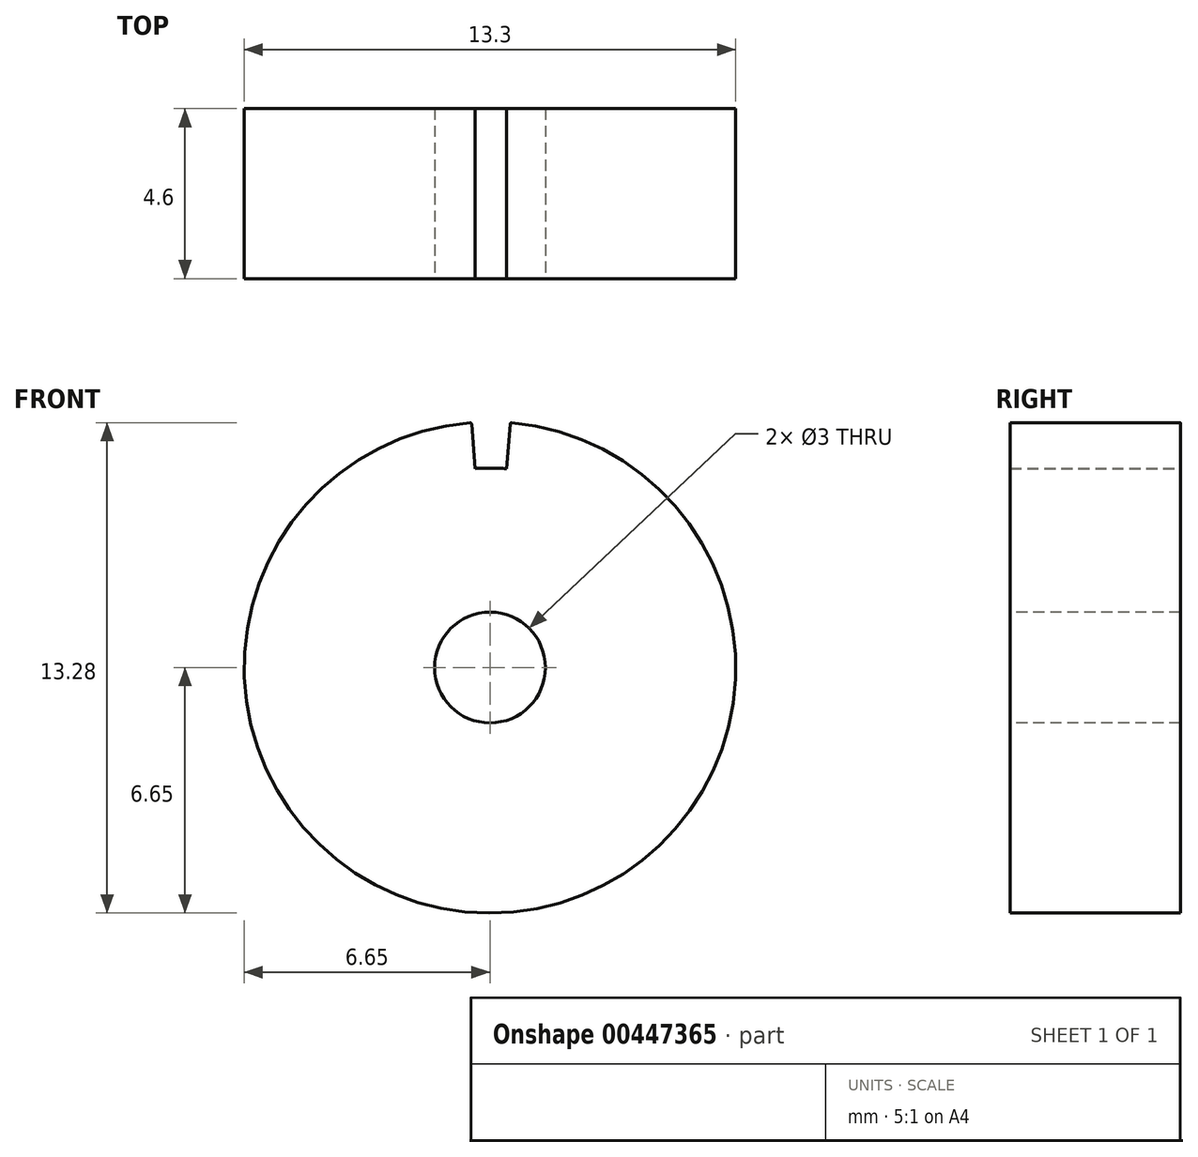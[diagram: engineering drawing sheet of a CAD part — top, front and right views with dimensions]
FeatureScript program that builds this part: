
annotation { "Feature Type Name" : "Feature", "Feature Type Description" : "" }
export const myFeature = defineFeature(function(context is Context, id is Id, definition is map)
    precondition{}
    {
        {
            var Q0;
            Q0=qCreatedBy(makeId("Right.planeOp"),FACE);
            var sketch = newSketch(context, id + "F0", { "sketchPlane" : qUnion([Q0])});
            skLineSegment(sketch, "E0.bottom", {"start": v(0, 1.5) * mm, "end": v(4.6, 1.5) * mm});
            skLineSegment(sketch, "E0.top", {"start": v(0, 6.65) * mm, "end": v(4.6, 6.65) * mm});
            skLineSegment(sketch, "E0.left", {"start": v(0, 1.5) * mm, "end": v(0, 6.65) * mm});
            skLineSegment(sketch, "E0.right", {"start": v(4.6, 1.5) * mm, "end": v(4.6, 6.65) * mm});
            skLineSegment(sketch, "E1", {"start": v(0, 0) * mm, "end": v(5, 0) * mm, "construction": true});
            skLineSegment(sketch, "E2.MirrorCS", {"start": v(0, -1.5) * mm, "end": v(4.6, -1.5) * mm});
            skLineSegment(sketch, "E3.MirrorCS", {"start": v(0, -6.65) * mm, "end": v(4.6, -6.65) * mm});
            skLineSegment(sketch, "E4.MirrorCS", {"start": v(0, -1.5) * mm, "end": v(0, -6.65) * mm});
            skLineSegment(sketch, "E5.MirrorCS", {"start": v(4.6, -1.5) * mm, "end": v(4.6, -6.65) * mm});
            skSolve(sketch);
        }
        {
            var Q0;
            Q0 = qSketchRegion(id + "F0", true);
            var Q1;
            {var subQ5=sQuery(id+"F0.wireOp",EDGE,"FwvJN74M-N8XB-vuCw-gHGy-UIWHDAiXAmXn.right");Q1=makeQuery(id+"F0.imprint","IMPRINT",FACE,{"disambiguationData":[TD([[makeQuery(id+"F0.imprint","IMPRINT",EDGE,{"derivedFrom":subQ5}),1.0]])]});}
            var Q2;
            {var subQ5=sQuery(id+"F0.wireOp",EDGE,"FwvJN74M-N8XB-vuCw-gHGy-UIWHDAiXAmXn.left");Q2=makeQuery(id+"F0.imprint","IMPRINT",FACE,{"disambiguationData":[TD([[makeQuery(id+"F0.imprint","IMPRINT",EDGE,{"derivedFrom":subQ5}),-1.0]])]});}
            var Q3;
            {var subQ0=sQuery(id+"F0.wireOp",EDGE,"E0.top");Q3=makeQuery(id+"F0.imprint","IMPRINT",FACE,{"disambiguationData":[TD([[makeQuery(id+"F0.imprint","IMPRINT",EDGE,{"derivedFrom":subQ0}),-1.0]])]});}
            var Q4;
            {var subQ0=sQuery(id+"F0.wireOp",EDGE,"FwvJN74M-N8XB-vuCw-gHGy-UIWHDAiXAmXn.bottom");var subQ1=sQuery(id+"F0.wireOp",EDGE,"E0.left");var subQ2=makeQuery(id+"F0.imprint","INTERSECT",VERTEX,{"derivedFrom":[subQ1,subQ0]});Q4=makeQuery(id+"F0.imprint","IMPRINT",FACE,{"disambiguationData":[TD([[makeQuery(id+"F0.imprint","IMPRINT",EDGE,{"disambiguationData":[TD([[subQ2,-1.0]])],"derivedFrom":subQ1}),-1.0]])]});}
            var Q5;
            Q5=sQuery(id+"F0.wireOp",EDGE,"E1");
            revolve(context, id + "F1", {"entities" : qUnion([Q0, Q1, Q2, Q3, Q4]), "axis" : qUnion([Q5]), "revolveType" : RevolveType.FULL});
        }
        {
            var Q0;
            Q0=makeQuery(id+"F1.opRevolve","SWEPT_FACE",FACE,{"disambiguationData":[OSD([sQuery(id+"F0.wireOp",EDGE,"E0.right")])]});
            var sketch = newSketch(context, id + "F2", { "sketchPlane" : qUnion([Q0])});
            skArc(sketch, "E6", {"start": v(0.4, 5.39) * mm, "mid": v(-0.02, 5.4) * mm, "end": v(-0.45, 5.38) * mm});
            skLineSegment(sketch, "E7", {"start": v(0, 0) * mm, "end": v(0, 7.57) * mm, "construction": true});
            skLineSegment(sketch, "E8", {"start": v(-0.54, 6.59) * mm, "end": v(-0.45, 5.38) * mm});
            skLineSegment(sketch, "E9", {"start": v(0.5, 6.6) * mm, "end": v(0.4, 5.39) * mm});
            skPoint(sketch, "E10.visualSharp", {"position": v(-0.55, 6.63) * mm});
            skArc(sketch, "E10.filletArc", {"start": v(-0.54, 6.59) * mm, "mid": v(-0.56, 6.61) * mm, "end": v(-0.59, 6.62) * mm});
            skPoint(sketch, "E11.visualSharp", {"position": v(0.5, 6.63) * mm});
            skArc(sketch, "E11.filletArc", {"start": v(0.54, 6.63) * mm, "mid": v(0.51, 6.62) * mm, "end": v(0.5, 6.6) * mm});
            skSolve(sketch);
        }
        {
            var Q0;
            Q0=makeQuery(id+"F2.imprint","IMPRINT",FACE,{"disambiguationData":[TD([[makeQuery(id+"F2.imprint","IMPRINT",EDGE,{"derivedFrom":sQuery(id+"F2.wireOp",EDGE,"E6")}),-1.0]])]});
            extrude(context, id + "F3", {"entities" : qUnion([Q0]), "operationType" : NewBodyOperationType.REMOVE, "endBound" : BoundingType.THROUGH_ALL, "oppositeDirection" : true, "depth" : 25 * mm});
        }
    });
